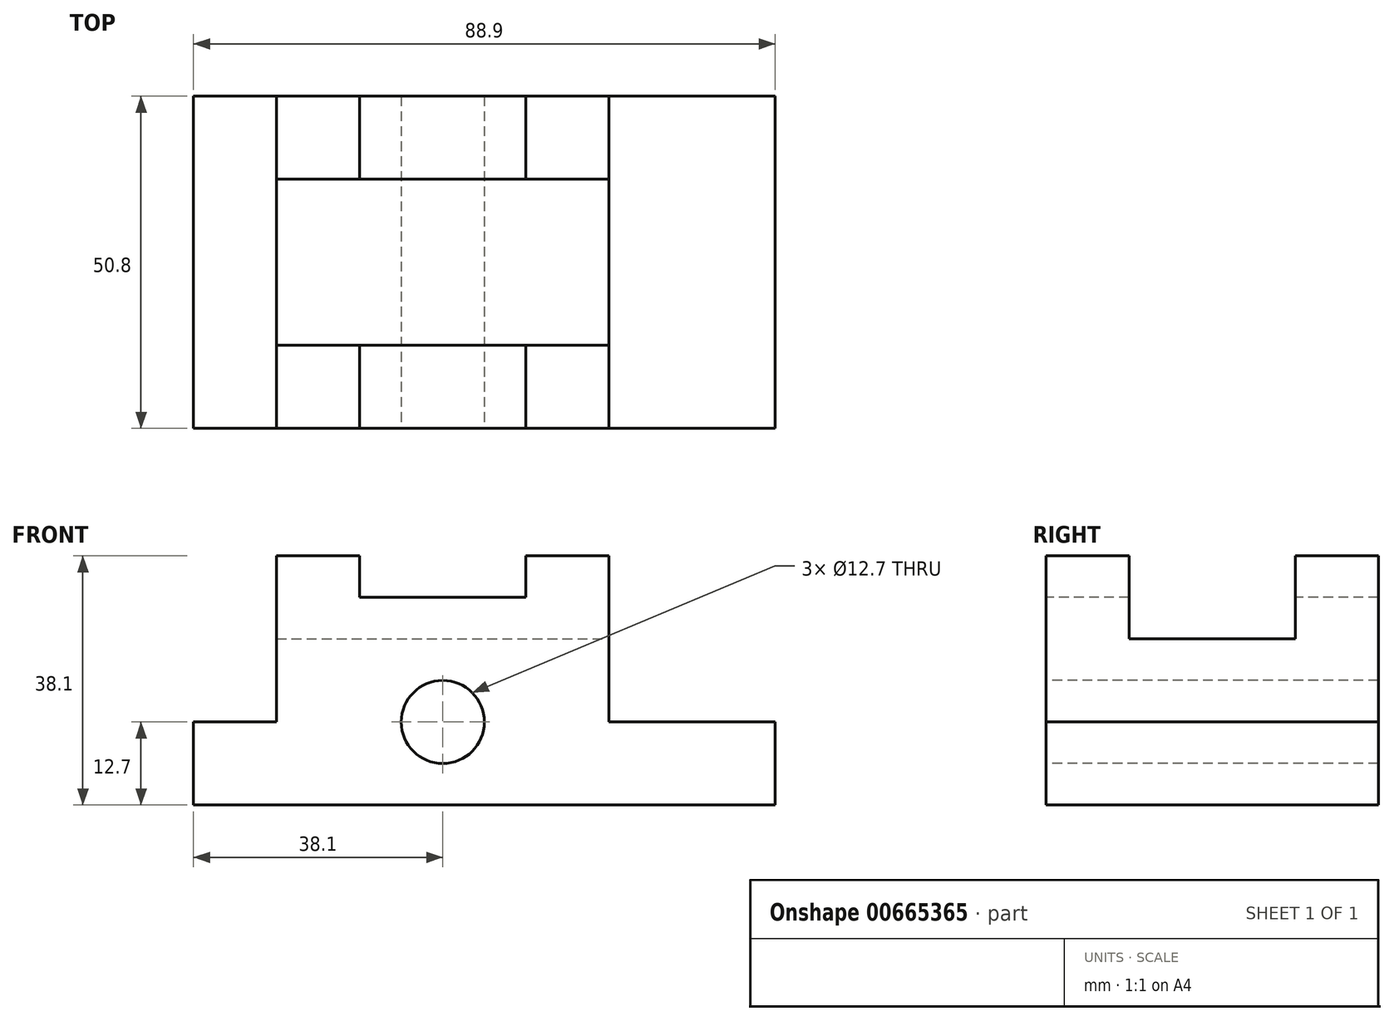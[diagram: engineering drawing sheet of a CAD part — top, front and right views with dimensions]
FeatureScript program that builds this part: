
annotation { "Feature Type Name" : "Feature", "Feature Type Description" : "" }
export const myFeature = defineFeature(function(context is Context, id is Id, definition is map)
    precondition{}
    {
        {
            var Q0;
            Q0=qCreatedBy(makeId("Front.planeOp"),FACE);
            var sketch = newSketch(context, id + "F0", { "sketchPlane" : qUnion([Q0])});
            skLineSegment(sketch, "E0.bottom", {"start": v(44.45, 19.05) * mm, "end": v(-44.45, 19.05) * mm});
            skLineSegment(sketch, "E0.top", {"start": v(44.45, -19.05) * mm, "end": v(-44.45, -19.05) * mm});
            skLineSegment(sketch, "E0.left", {"start": v(44.45, 19.05) * mm, "end": v(44.45, -19.05) * mm});
            skLineSegment(sketch, "E0.right", {"start": v(-44.45, 19.05) * mm, "end": v(-44.45, -19.05) * mm});
            skPoint(sketch, "E0.middle", {"position": v(0, 0) * mm});
            skSolve(sketch);
        }
        {
            var Q0;
            Q0=makeQuery(id+"F0.imprint","IMPRINT",FACE,{"disambiguationData":[TD([[makeQuery(id+"F0.imprint","IMPRINT",EDGE,{"derivedFrom":sQuery(id+"F0.wireOp",EDGE,"E0.bottom")}),1.0]])]});
            extrude(context, id + "F1", {"entities" : qUnion([Q0]), "depth" : 50.8 * mm, "offsetDistance" : 25.4 * mm});
        }
        {
            var Q0;
            Q0=makeQuery(id+"F1.opExtrude","CAP_FACE",FACE,{"disambiguationData":[OSD([sQuery(id+"F0.wireOp",EDGE,"E0.bottom"),sQuery(id+"F0.wireOp",EDGE,"E0.top"),sQuery(id+"F0.wireOp",EDGE,"E0.left"),sQuery(id+"F0.wireOp",EDGE,"E0.right")])],"isStart":false});
            var sketch = newSketch(context, id + "F2", { "sketchPlane" : qUnion([Q0])});
            skLineSegment(sketch, "E1.bottom", {"start": v(-44.45, 19.05) * mm, "end": v(-31.75, 19.05) * mm});
            skLineSegment(sketch, "E1.top", {"start": v(-44.45, -6.35) * mm, "end": v(-31.75, -6.35) * mm});
            skLineSegment(sketch, "E1.left", {"start": v(-44.45, 19.05) * mm, "end": v(-44.45, -6.35) * mm});
            skLineSegment(sketch, "E1.right", {"start": v(-31.75, 19.05) * mm, "end": v(-31.75, -6.35) * mm});
            skSolve(sketch);
        }
        {
            var Q0;
            Q0=makeQuery(id+"F2.imprint","IMPRINT",FACE,{"disambiguationData":[TD([[makeQuery(id+"F2.imprint","IMPRINT",EDGE,{"derivedFrom":sQuery(id+"F2.wireOp",EDGE,"E1.bottom")}),1.0]])]});
            extrude(context, id + "F3", {"entities" : qUnion([Q0]), "operationType" : NewBodyOperationType.REMOVE, "endBound" : BoundingType.THROUGH_ALL, "oppositeDirection" : true, "depth" : 25.4 * mm, "offsetDistance" : 25.4 * mm});
        }
        {
            var Q0;
            Q0=makeQuery(id+"F1.opExtrude","CAP_FACE",FACE,{"disambiguationData":[OSD([sQuery(id+"F0.wireOp",EDGE,"E0.bottom"),sQuery(id+"F0.wireOp",EDGE,"E0.top"),sQuery(id+"F0.wireOp",EDGE,"E0.left"),sQuery(id+"F0.wireOp",EDGE,"E0.right")])],"isStart":false});
            var sketch = newSketch(context, id + "F4", { "sketchPlane" : qUnion([Q0])});
            skLineSegment(sketch, "E2.bottom", {"start": v(-19.05, 19.05) * mm, "end": v(6.35, 19.05) * mm});
            skLineSegment(sketch, "E2.top", {"start": v(-19.05, 12.7) * mm, "end": v(6.35, 12.7) * mm});
            skLineSegment(sketch, "E2.left", {"start": v(-19.05, 19.05) * mm, "end": v(-19.05, 12.7) * mm});
            skLineSegment(sketch, "E2.right", {"start": v(6.35, 19.05) * mm, "end": v(6.35, 12.7) * mm});
            skSolve(sketch);
        }
        {
            var Q0;
            Q0=makeQuery(id+"F4.imprint","IMPRINT",FACE,{"disambiguationData":[TD([[makeQuery(id+"F4.imprint","IMPRINT",EDGE,{"derivedFrom":sQuery(id+"F4.wireOp",EDGE,"E2.bottom")}),1.0]])]});
            extrude(context, id + "F5", {"entities" : qUnion([Q0]), "operationType" : NewBodyOperationType.REMOVE, "endBound" : BoundingType.THROUGH_ALL, "oppositeDirection" : true, "depth" : 25.4 * mm, "offsetDistance" : 25.4 * mm});
        }
        {
            var Q0;
            Q0=makeQuery(id+"F1.opExtrude","CAP_FACE",FACE,{"disambiguationData":[OSD([sQuery(id+"F0.wireOp",EDGE,"E0.bottom"),sQuery(id+"F0.wireOp",EDGE,"E0.top"),sQuery(id+"F0.wireOp",EDGE,"E0.left"),sQuery(id+"F0.wireOp",EDGE,"E0.right")])],"isStart":false});
            var sketch = newSketch(context, id + "F6", { "sketchPlane" : qUnion([Q0])});
            skLineSegment(sketch, "E3.bottom", {"start": v(19.05, 19.05) * mm, "end": v(44.45, 19.05) * mm});
            skLineSegment(sketch, "E3.top", {"start": v(19.05, -6.35) * mm, "end": v(44.45, -6.35) * mm});
            skLineSegment(sketch, "E3.left", {"start": v(19.05, 19.05) * mm, "end": v(19.05, -6.35) * mm});
            skLineSegment(sketch, "E3.right", {"start": v(44.45, 19.05) * mm, "end": v(44.45, -6.35) * mm});
            skSolve(sketch);
        }
        {
            var Q0;
            Q0=makeQuery(id+"F6.imprint","IMPRINT",FACE,{"disambiguationData":[TD([[makeQuery(id+"F6.imprint","IMPRINT",EDGE,{"derivedFrom":sQuery(id+"F6.wireOp",EDGE,"E3.bottom")}),1.0]])]});
            extrude(context, id + "F7", {"entities" : qUnion([Q0]), "operationType" : NewBodyOperationType.REMOVE, "endBound" : BoundingType.THROUGH_ALL, "oppositeDirection" : true, "depth" : 25.4 * mm, "offsetDistance" : 25.4 * mm});
        }
        {
            var Q0;
            Q0=makeQuery(id+"F7.boolean.opBoolean","COPY",FACE,{"derivedFrom":makeQuery(id+"F7.opExtrude","SWEPT_FACE",FACE,{"disambiguationData":[OSD([sQuery(id+"F6.wireOp",EDGE,"E3.left")])]})});
            var sketch = newSketch(context, id + "F8", { "sketchPlane" : qUnion([Q0])});
            skLineSegment(sketch, "E4.bottom", {"start": v(-38.1, 19.05) * mm, "end": v(-12.7, 19.05) * mm});
            skLineSegment(sketch, "E4.top", {"start": v(-38.1, 6.35) * mm, "end": v(-12.7, 6.35) * mm});
            skLineSegment(sketch, "E4.left", {"start": v(-38.1, 19.05) * mm, "end": v(-38.1, 6.35) * mm});
            skLineSegment(sketch, "E4.right", {"start": v(-12.7, 19.05) * mm, "end": v(-12.7, 6.35) * mm});
            skSolve(sketch);
        }
        {
            var Q0;
            Q0=makeQuery(id+"F8.imprint","IMPRINT",FACE,{"disambiguationData":[TD([[makeQuery(id+"F8.imprint","IMPRINT",EDGE,{"derivedFrom":sQuery(id+"F8.wireOp",EDGE,"E4.bottom")}),1.0]])]});
            extrude(context, id + "F9", {"entities" : qUnion([Q0]), "operationType" : NewBodyOperationType.REMOVE, "endBound" : BoundingType.THROUGH_ALL, "oppositeDirection" : true, "depth" : 25.4 * mm, "offsetDistance" : 25.4 * mm});
        }
        {
            var Q0;
            Q0=makeQuery(id+"F1.opExtrude","CAP_FACE",FACE,{"disambiguationData":[OSD([sQuery(id+"F0.wireOp",EDGE,"E0.bottom"),sQuery(id+"F0.wireOp",EDGE,"E0.top"),sQuery(id+"F0.wireOp",EDGE,"E0.left"),sQuery(id+"F0.wireOp",EDGE,"E0.right")])],"isStart":false});
            var sketch = newSketch(context, id + "F10", { "sketchPlane" : qUnion([Q0])});
            skCircle(sketch, "E5", {"center": v(-6.35, -6.35) * mm, "radius": 6.35 * mm});
            skSolve(sketch);
        }
        {
            var Q0;
            Q0=makeQuery(id+"F10.imprint","IMPRINT",FACE,{"disambiguationData":[TD([[makeQuery(id+"F10.imprint","IMPRINT",EDGE,{"derivedFrom":sQuery(id+"F10.wireOp",EDGE,"E5")}),1.0]])]});
            extrude(context, id + "F11", {"entities" : qUnion([Q0]), "operationType" : NewBodyOperationType.REMOVE, "endBound" : BoundingType.THROUGH_ALL, "oppositeDirection" : true, "depth" : 25.4 * mm, "offsetDistance" : 25.4 * mm});
        }
    });
